# Revit family: EdgeProtection_Gutters_Schluter_Bara_RK
name_source: partatom
category: Profiles
units: mm (PartAtom-declared; Revit-internal decimal feet)

## family parameters
OmniClass Number = 23.35.50.11.21.17
OmniClass Title = Underlays, Linings, Separations
Profile Usage = <Generic>
Rotate with component = No
Section Shape = Not Defined

## types (1)
- EdgeProtection_Gutters_Schluter_Bara_RK
    Assembly Code = C3020430
    Construction Details = http://www.arcat.com
    Description = As Specified in 09 30 00
    Expected Lifespan (Years) = 0
    Green Building-LEED = http://www.arcat.com
    Installation-Fabrication = http://www.schluter.com
    Keynote = 09 30 00
    Maintenance Schedule (Months) = 0
    Manufacturer = Schluter System LP
    Manufacturer Fax = 800-477-9783
    Manufacturer Website = http://www.schluter.com
    Model = As Specified in 09 30 00
    Product Data = http://www.arcat.com
    Product Properties = http://www.arcat.com
    Sales Information = http://www.schluter.com
    Send Message = http://www.arcat.com
    SpecWizard = http://www.arcat.com
    Specification = http://www.arcat.com
    Test Data = D
    URL = http://www.schluter.com
    Warranty Duration (Years) = 0

## geometry (parser evidence)
native form markers: Sweep x1
no freeform markers — native parametric forms only
